# Revit family: KEUCO_14954010100
name_source: partatom
category: Allgemeines Modell
revit_build: Autodesk Revit 2016 (Build: 20150220_1215(x64)
units: mm (PartAtom-declared; Revit-internal decimal feet)

## family parameters
Arbeitsebenenbasiert = Ja
Beim Laden mit Abzugskörper schneiden = Nein
Bemaßung runder Anschluss = Durchmesser verwenden
Gemeinsam genutzt = Nein
Immer vertikal = Nein
Kann Basisbauteil für Bewehrung sein = Nein
Raumberechnungspunkt = Nein
Teiletyp = Normal

## types (3) — shared parameters
Beschreibung = mit Kunststoff-Behälter und Pumpe
Füllmenge: ca. 1,1 l
Dosiermenge: ca. 2,5 ml/Hub
Gewicht = 2.718
Hersteller = KEUCO
Kategorie = ACC
Material Oben = Schwarzgrau
Rail Length = 851 mm  [stored 2.79199 ft]
Serie = Plan
URL = https://www.keuco.com
Verwendung = WP
Vorgabe-Ansicht = 1219 mm

## per-type parameters (varying)
| type | Artikelnummer | Ausschreibungstext | Stange Material |
| 14954010100 | 14954010100
14985010000 | KEUCO PLAN Lotionspender 14954010100
Hochglanzverchromter Lotionspender, Wandmodell 
in ästhetischem, funktionalem Design 
leichtes Reinigen und leichtes Befüllen 
diebstahlgesichert für Montage im öffentlichen Bereich 
Füllmenge ca. 1,1 l, für handelsübliche Flüssigseifen 
Dosiermenge ca. 2,5 ml/Hub 
Grundkörperdurchmesser 104 mm, Höhe 271 mm , Ausladung 115 mm 
Der Lotionspender wird verdeckt angebracht.
Lieferung inkl. korrosionsfreiem Befestigungsmaterial
Zur Montage im Duschbereich bitte zusätzlich den Dichtungsdeckel
Artikel-Nr. 14954 bestellen! | Verchromt |
| 14954170100 | 14954170100
14985010000 | KEUCO PLAN Lotionspender 14954170100 
Lotionspender aus silber-eloxiertem Aluminium (E6 EV1) 
Wandmodell, in ästhetischem, funktionalem Design 
leichtes Reinigen und leichtes Befüllen 
diebstahlgesichert für Montage im öffentlichen Bereich 
Füllmenge ca 1,1 l, für handelsübliche Flüssigseifen 
Dosiermenge ca. 2,5 ml/Hub 
Grundkörperdurchmesser 104 mm, Höhe 271 mm , Ausladung 115 mm 
Der Lotionspender wird verdeckt angebracht
Lieferung inkl. korrosionsfreiem Befestigungsmaterial
Zur Montage im Duschbereich bitte zusätzlich den Dichtungsdeckel
Artikel-Nr. 14954 bestellen! | Aluminium silber-eloxiert (E6 EV1) |
| 14954070100 | 14954070100 | KEUCO PLAN Lotionspender 14954070100 
Lotionspender aus hochwertigem Edelstahl, Wandmodell
in ästhetischem, funktionalem Design 
leichtes Reinigen und leichtes Befüllen 
diebstahlgesichert für Montage im öffentlichen Bereich 
Füllmenge ca. 1,1 l, für handelsübliche Flüssigseifen 
Dosiermenge ca. 2,5 ml/Hub 
Grundkörperdurchmesser 104 mm, Höhe 271 mm , Ausladung 115 mm 
Der Lotionspender wird verdeckt angebracht.
Lieferung inkl. korrosionsfreiem Befestigungsmaterial
Zur Montage im Duschbereich bitte zusätzlich den Dichtungsdeckel
Artikel-Nr. 14954 bestellen! | Verchromt |

note: [stored X ft] marks values corroborated as IEEE doubles in the binary element streams (Revit-internal decimal feet)

## geometry (parser evidence)
native form markers: Sweep x3
no freeform markers — native parametric forms only
